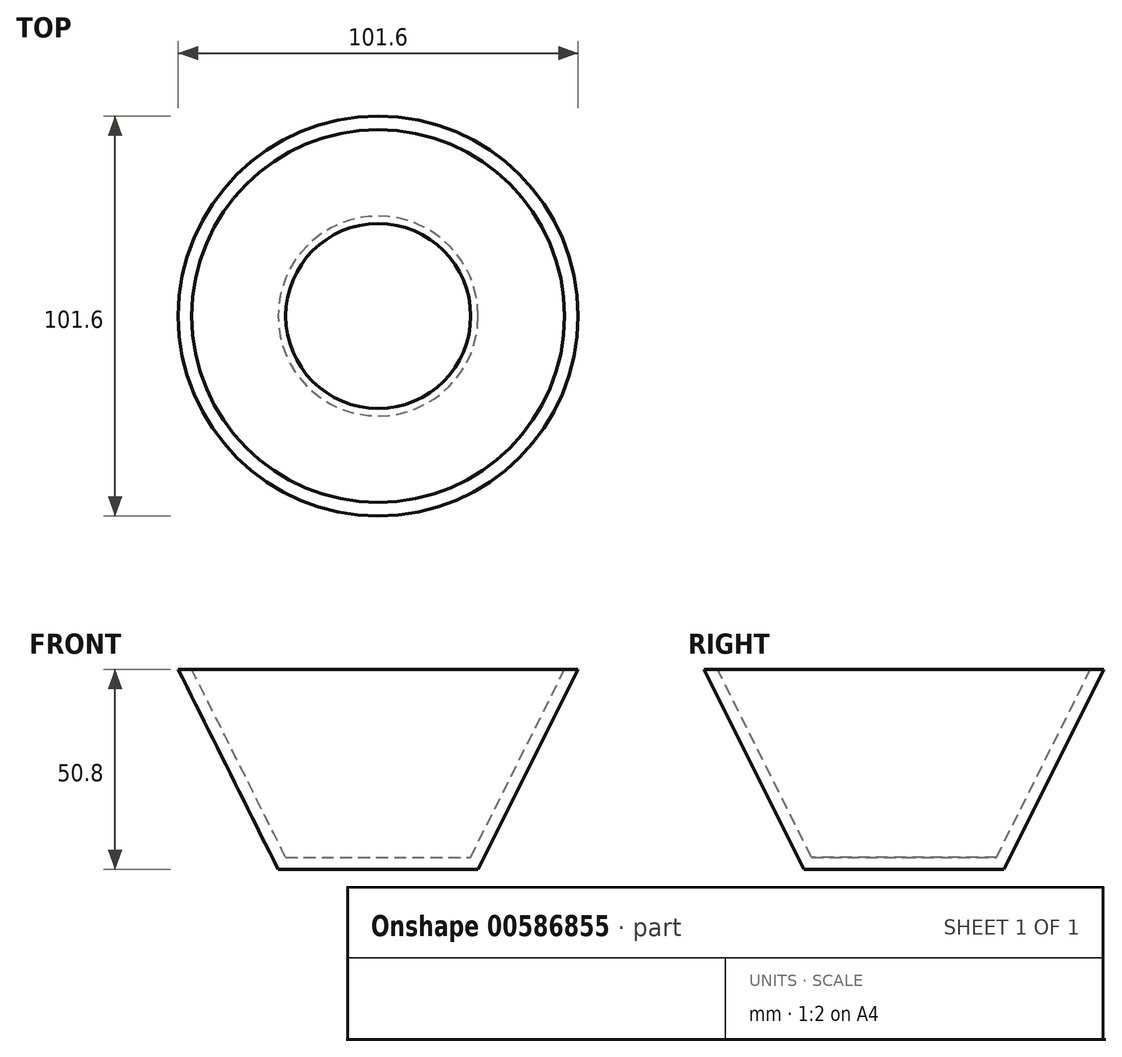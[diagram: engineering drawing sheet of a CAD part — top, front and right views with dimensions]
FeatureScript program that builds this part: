
annotation { "Feature Type Name" : "Feature", "Feature Type Description" : "" }
export const myFeature = defineFeature(function(context is Context, id is Id, definition is map)
    precondition{}
    {
        {
            var Q0;
            Q0=qCreatedBy(makeId("Front.planeOp"),FACE);
            var sketch = newSketch(context, id + "F0", { "sketchPlane" : qUnion([Q0])});
            skLineSegment(sketch, "E0", {"start": v(0, 0) * mm, "end": v(0, 50.8) * mm, "construction": true});
            skLineSegment(sketch, "E1", {"start": v(0, 0) * mm, "end": v(25.4, 0) * mm});
            skLineSegment(sketch, "E2", {"start": v(25.4, 0) * mm, "end": v(50.8, 50.8) * mm});
            skLineSegment(sketch, "E3.0", {"start": v(23.5, 3.07) * mm, "end": v(47.36, 50.8) * mm});
            skLineSegment(sketch, "E3.1", {"start": v(0, 3.07) * mm, "end": v(23.5, 3.07) * mm});
            skLineSegment(sketch, "E4", {"start": v(47.36, 50.8) * mm, "end": v(50.8, 50.8) * mm});
            skLineSegment(sketch, "E5", {"start": v(0, 0) * mm, "end": v(0, 3.07) * mm});
            skSolve(sketch);
        }
        {
            var Q0;
            Q0=makeQuery(id+"F0.imprint","IMPRINT",FACE,{"disambiguationData":[TD([[makeQuery(id+"F0.imprint","IMPRINT",EDGE,{"derivedFrom":sQuery(id+"F0.wireOp",EDGE,"E1")}),1.0]])]});
            var Q1;
            Q1=sQuery(id+"F0.wireOp",EDGE,"E0");
            revolve(context, id + "F1", {"entities" : qUnion([Q0]), "axis" : qUnion([Q1]), "revolveType" : RevolveType.FULL});
        }
    });
